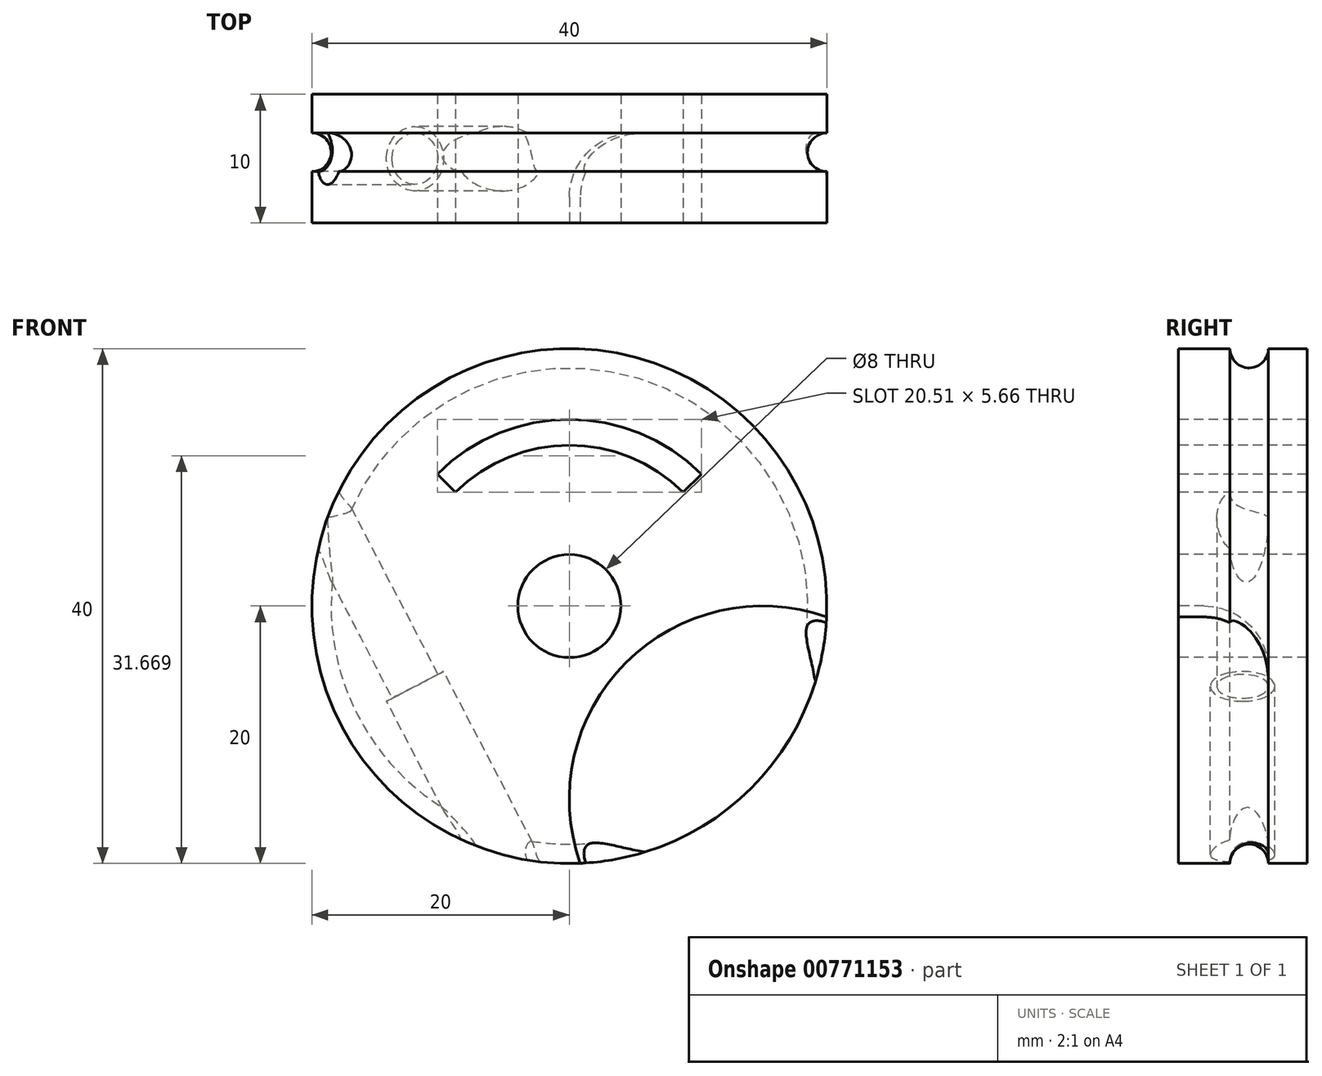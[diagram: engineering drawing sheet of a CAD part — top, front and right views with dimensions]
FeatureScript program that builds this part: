
annotation { "Feature Type Name" : "Feature", "Feature Type Description" : "" }
export const myFeature = defineFeature(function(context is Context, id is Id, definition is map)
    precondition{}
    {
        {
            var Q0;
            Q0=qCreatedBy(makeId("Front.planeOp"),FACE);
            var sketch = newSketch(context, id + "F0", { "sketchPlane" : qUnion([Q0])});
            skCircle(sketch, "E0", {"center": v(0, 0) * mm, "radius": 20 * mm});
            skCircle(sketch, "E1", {"center": v(0, 0) * mm, "radius": 10 * mm});
            skCircle(sketch, "E2", {"center": v(0, 0) * mm, "radius": 4 * mm});
            skCircle(sketch, "E3", {"center": v(0, 0) * mm, "radius": 18 * mm});
            skSolve(sketch);
        }
        {
            var Q0;
            Q0=makeQuery(id+"F0.imprint","IMPRINT",FACE,{"disambiguationData":[TD([[makeQuery(id+"F0.imprint","IMPRINT",EDGE,{"derivedFrom":sQuery(id+"F0.wireOp",EDGE,"E0")}),1.0]])]});
            var Q1;
            Q1=makeQuery(id+"F0.imprint","IMPRINT",FACE,{"disambiguationData":[TD([[makeQuery(id+"F0.imprint","IMPRINT",EDGE,{"derivedFrom":sQuery(id+"F0.wireOp",EDGE,"E1")}),1.0]])]});
            var Q2;
            Q2=makeQuery(id+"F0.imprint","IMPRINT",FACE,{"disambiguationData":[TD([[makeQuery(id+"F0.imprint","IMPRINT",EDGE,{"derivedFrom":sQuery(id+"F0.wireOp",EDGE,"E1")}),-1.0]])]});
            var Q3;
            Q3=makeQuery(id+"F0.imprint","IMPRINT",FACE,{"disambiguationData":[TD([[makeQuery(id+"F0.imprint","IMPRINT",EDGE,{"derivedFrom":sQuery(id+"F0.wireOp",EDGE,"E0")}),1.0]])]});
            extrude(context, id + "F1", {"entities" : qUnion([Q0, Q1, Q2, Q3]), "oppositeDirection" : true, "depth" : 3 * mm, "offsetDistance" : 25 * mm});
        }
        {
            var Q0;
            Q0=makeQuery(id+"F0.imprint","IMPRINT",FACE,{"disambiguationData":[TD([[makeQuery(id+"F0.imprint","IMPRINT",EDGE,{"derivedFrom":sQuery(id+"F0.wireOp",EDGE,"E0")}),1.0]])]});
            var Q1;
            Q1=makeQuery(id+"F0.imprint","IMPRINT",FACE,{"disambiguationData":[TD([[makeQuery(id+"F0.imprint","IMPRINT",EDGE,{"derivedFrom":sQuery(id+"F0.wireOp",EDGE,"E1")}),-1.0]])]});
            var Q2;
            Q2=makeQuery(id+"F0.imprint","IMPRINT",FACE,{"disambiguationData":[TD([[makeQuery(id+"F0.imprint","IMPRINT",EDGE,{"derivedFrom":sQuery(id+"F0.wireOp",EDGE,"E1")}),1.0]])]});
            extrude(context, id + "F2", {"entities" : qUnion([Q0, Q1, Q2]), "operationType" : NewBodyOperationType.ADD, "oppositeDirection" : true, "depth" : 3 * mm, "offsetDistance" : 25 * mm});
        }
        {
            var Q0;
            Q0=qCreatedBy(makeId("Front.planeOp"),FACE);
            cPlane(context, id + "F3", {"entities" : qUnion([Q0]), "cplaneType" : CPlaneType.OFFSET, "offset" : 15 * mm, "oppositeDirection" : true, "width" : 150 * mm, "height" : 150 * mm});
        }
        {
            var Q0;
            Q0=qCreatedBy(id+"F3.planeOp",FACE);
            var sketch = newSketch(context, id + "F4", { "sketchPlane" : qUnion([Q0])});
            skPoint(sketch, "E4.0", {"position": v(0, 0) * mm});
            skCircle(sketch, "E5.0", {"center": v(0, 0) * mm, "radius": 10 * mm});
            skCircle(sketch, "E5.1", {"center": v(0, 0) * mm, "radius": 20 * mm});
            skLineSegment(sketch, "E6", {"start": v(0, 10) * mm, "end": v(0, 115) * mm});
            skArc(sketch, "E7", {"start": v(55, 165) * mm, "mid": v(16.44, 152.17) * mm, "end": v(0, 115) * mm});
            skLineSegment(sketch, "E8", {"start": v(0, 115) * mm, "end": v(50.23, 115) * mm, "construction": true});
            skLineSegment(sketch, "E9", {"start": v(0, 115) * mm, "end": v(0, 165) * mm, "construction": true});
            skLineSegment(sketch, "E10", {"start": v(55, 165) * mm, "end": v(0, 165) * mm, "construction": true});
            skSolve(sketch);
        }
        {
            var Q0;
            Q0=qCreatedBy(makeId("Top.planeOp"),FACE);
            cPlane(context, id + "F5", {"entities" : qUnion([Q0]), "cplaneType" : CPlaneType.OFFSET, "offset" : 8 * mm, "width" : 150 * mm, "height" : 150 * mm});
        }
        {
            var Q0;
            Q0=makeQuery(id+"F0.imprint","IMPRINT",FACE,{"disambiguationData":[TD([[makeQuery(id+"F0.imprint","IMPRINT",EDGE,{"derivedFrom":sQuery(id+"F0.wireOp",EDGE,"E0")}),1.0]])]});
            var Q1;
            Q1=makeQuery(id+"F0.imprint","IMPRINT",FACE,{"disambiguationData":[TD([[makeQuery(id+"F0.imprint","IMPRINT",EDGE,{"derivedFrom":sQuery(id+"F0.wireOp",EDGE,"E1")}),-1.0]])]});
            var Q2;
            Q2=makeQuery(id+"F0.imprint","IMPRINT",FACE,{"disambiguationData":[TD([[makeQuery(id+"F0.imprint","IMPRINT",EDGE,{"derivedFrom":sQuery(id+"F0.wireOp",EDGE,"E1")}),1.0]])]});
            extrude(context, id + "F6", {"entities" : qUnion([Q0, Q1, Q2]), "operationType" : NewBodyOperationType.ADD, "depth" : 7 * mm, "offsetDistance" : 25 * mm});
        }
        {
            var Q0;
            Q0=qCreatedBy(makeId("Right.planeOp"),FACE);
            var sketch = newSketch(context, id + "F7", { "sketchPlane" : qUnion([Q0])});
            skCircle(sketch, "E11", {"center": v(-1.5, 20) * mm, "radius": 1.5 * mm});
            skSolve(sketch);
        }
        {
            var Q0;
            Q0=makeQuery(id+"F7.imprint","IMPRINT",FACE,{"disambiguationData":[TD([[makeQuery(id+"F7.imprint","IMPRINT",EDGE,{"derivedFrom":sQuery(id+"F7.wireOp",EDGE,"E11")}),1.0]])]});
            var Q1;
            Q1=makeQuery(id+"F6.opExtrude","CAP_EDGE",EDGE,{"disambiguationData":[OSD([sQuery(id+"F0.wireOp",EDGE,"E0")])],"isStart":false});
            revolve(context, id + "F8", {"operationType" : NewBodyOperationType.REMOVE, "surfaceOperationType" : NewSurfaceOperationType.NEW, "entities" : qUnion([Q0]), "axis" : qUnion([Q1]), "revolveType" : RevolveType.FULL, "oppositeDirection" : true});
        }
        {
            var Q0;
            Q0=makeQuery(id+"F6.opExtrude","CAP_FACE",FACE,{"disambiguationData":[OSD([sQuery(id+"F0.wireOp",EDGE,"E0"),sQuery(id+"F0.wireOp",EDGE,"E2")])],"isStart":false});
            cPlane(context, id + "F9", {"entities" : qUnion([Q0]), "cplaneType" : CPlaneType.OFFSET, "offset" : 0 * mm, "width" : 150 * mm, "height" : 150 * mm});
        }
        {
            var Q0;
            Q0=qCreatedBy(id+"F9.planeOp",FACE);
            var sketch = newSketch(context, id + "F10", { "sketchPlane" : qUnion([Q0])});
            skCircle(sketch, "E12", {"center": v(15, -15) * mm, "radius": 15 * mm});
            skLineSegment(sketch, "E13", {"start": v(0, 0) * mm, "end": v(50, 0) * mm});
            skLineSegment(sketch, "E14", {"start": v(0, 0) * mm, "end": v(0, -50) * mm});
            skCircle(sketch, "E15", {"center": v(0, 0) * mm, "radius": 12.5 * mm});
            skCircle(sketch, "E16", {"center": v(0, 0) * mm, "radius": 14.5 * mm});
            skLineSegment(sketch, "E17", {"start": v(0, 0) * mm, "end": v(-14.14, 14.14) * mm});
            skLineSegment(sketch, "E18", {"start": v(0, 0) * mm, "end": v(14.14, 14.14) * mm});
            skSolve(sketch);
        }
        {
            var Q0;
            Q0=qCreatedBy(id+"F9.planeOp",FACE);
            var sketch = newSketch(context, id + "F11", { "sketchPlane" : qUnion([Q0])});
            skLineSegment(sketch, "E19", {"start": v(0, 0) * mm, "end": v(-12.94, -48.3) * mm});
            skLineSegment(sketch, "E20", {"start": v(0, 0) * mm, "end": v(-46.98, 17.1) * mm});
            skCircle(sketch, "E21.0", {"center": v(0, 0) * mm, "radius": 20 * mm});
            skLineSegment(sketch, "E22", {"start": v(-18.8, 6.84) * mm, "end": v(-5.18, -19.32) * mm});
            skSolve(sketch);
        }
        {
            var Q0;
            Q0=qCreatedBy(id+"F9.planeOp",FACE);
            cPlane(context, id + "F12", {"entities" : qUnion([Q0]), "cplaneType" : CPlaneType.OFFSET, "offset" : 5 * mm, "oppositeDirection" : true, "width" : 150 * mm, "height" : 150 * mm});
        }
        {
            var Q0;
            Q0=qCreatedBy(id+"F12.planeOp",FACE);
            var sketch = newSketch(context, id + "F13", { "sketchPlane" : qUnion([Q0])});
            skPoint(sketch, "E23.0", {"position": v(-18.8, 6.84) * mm});
            skPoint(sketch, "E24.0", {"position": v(-5.18, -19.32) * mm});
            skLineSegment(sketch, "E25.0", {"start": v(-18.8, 6.84) * mm, "end": v(-5.18, -19.32) * mm});
            skSolve(sketch);
        }
        {
            var Q0;
            Q0=sQuery(id+"F13.wireOp",EDGE,"E25.0");
            cPlane(context, id + "F14", {"entities" : qUnion([Q0]), "cplaneType" : CPlaneType.MID_PLANE, "offset" : 25 * mm, "width" : 150 * mm, "height" : 150 * mm});
        }
        {
            var Q0;
            Q0=qCreatedBy(id+"F14.planeOp",FACE);
            var sketch = newSketch(context, id + "F15", { "sketchPlane" : qUnion([Q0])});
            skPoint(sketch, "E26.0", {"position": v(-13.51, 2) * mm});
            skCircle(sketch, "E27", {"center": v(-13.51, 2) * mm, "radius": 2 * mm});
            skCircle(sketch, "E28", {"center": v(-13.51, 2) * mm, "radius": 2.5 * mm});
            skSolve(sketch);
        }
        {
            var Q0;
            Q0=makeQuery(id+"F15.imprint","IMPRINT",FACE,{"disambiguationData":[TD([[makeQuery(id+"F15.imprint","IMPRINT",EDGE,{"derivedFrom":sQuery(id+"F15.wireOp",EDGE,"E27")}),1.0]])]});
            extrude(context, id + "F16", {"entities" : qUnion([Q0]), "operationType" : NewBodyOperationType.REMOVE, "oppositeDirection" : true, "depth" : 40 * mm, "offsetDistance" : 25 * mm, "symmetric" : true});
        }
        {
            var Q0;
            Q0=makeQuery(id+"F15.imprint","IMPRINT",FACE,{"disambiguationData":[TD([[makeQuery(id+"F15.imprint","IMPRINT",EDGE,{"derivedFrom":sQuery(id+"F15.wireOp",EDGE,"E27")}),-1.0]])]});
            var Q1;
            Q1=sQuery(id+"F15.wireOp",EDGE,"E28");
            var Q2;
            Q2=sQuery(id+"F15.wireOp",EDGE,"E27");
            extrude(context, id + "F17", {"entities" : qUnion([Q0]), "operationType" : NewBodyOperationType.REMOVE, "surfaceEntities" : qUnion([Q1, Q2]), "depth" : 25 * mm, "offsetDistance" : 25 * mm});
        }
        {
            var Q0;
            {var subQ0=sQuery(id+"F10.wireOp",EDGE,"E18");var subQ1=sQuery(id+"F10.wireOp",EDGE,"E15");var subQ2=makeQuery(id+"F10.imprint","INTERSECT",VERTEX,{"derivedFrom":[subQ1,subQ0]});Q0=makeQuery(id+"F10.imprint","IMPRINT",FACE,{"disambiguationData":[TD([[makeQuery(id+"F10.imprint","IMPRINT",EDGE,{"disambiguationData":[TD([[subQ2,-1.0]])],"derivedFrom":subQ1}),-1.0]])]});}
            extrude(context, id + "F18", {"entities" : qUnion([Q0]), "operationType" : NewBodyOperationType.REMOVE, "endBound" : BoundingType.THROUGH_ALL, "oppositeDirection" : true, "depth" : 25 * mm, "offsetDistance" : 25 * mm});
        }
        {
            var Q0;
            {var subQ0=sQuery(id+"F10.wireOp",EDGE,"815154f5-1ca3-4dbd-a51d-8ff744def0ee.0");var subQ1=sQuery(id+"F10.wireOp",EDGE,"E12");var subQ8=makeQuery(id+"F10.imprint","INTERSECT",VERTEX,{"disambiguationData":[OD(0.0)],"derivedFrom":[subQ1,subQ0]});Q0=makeQuery(id+"F10.imprint","IMPRINT",FACE,{"disambiguationData":[TD([[makeQuery(id+"F10.imprint","IMPRINT",EDGE,{"disambiguationData":[TD([[subQ8,-1.0]])],"derivedFrom":subQ1}),1.0]])]});}
            var Q1;
            {var subQ0=sQuery(id+"F10.wireOp",EDGE,"E15");var subQ1=sQuery(id+"F10.wireOp",EDGE,"E12");var subQ2=makeQuery(id+"F10.imprint","INTERSECT",VERTEX,{"disambiguationData":[OD(0.0)],"derivedFrom":[subQ1,subQ0]});Q1=makeQuery(id+"F10.imprint","IMPRINT",FACE,{"disambiguationData":[TD([[makeQuery(id+"F10.imprint","IMPRINT",EDGE,{"disambiguationData":[TD([[subQ2,-1.0]])],"derivedFrom":subQ1}),1.0]])]});}
            var Q2;
            {var subQ0=sQuery(id+"F10.wireOp",EDGE,"E12");var subQ1=makeQuery(id+"F10.imprint","INTERSECT",VERTEX,{"derivedFrom":[subQ0,sQuery(id+"F10.wireOp",EDGE,"E13")]});Q2=makeQuery(id+"F10.imprint","IMPRINT",FACE,{"disambiguationData":[TD([[makeQuery(id+"F10.imprint","IMPRINT",EDGE,{"disambiguationData":[TD([[subQ1,-1.0]])],"derivedFrom":subQ0}),1.0]])]});}
            var Q3;
            {var subQ0=sQuery(id+"F10.wireOp",EDGE,"E16");var subQ1=sQuery(id+"F10.wireOp",EDGE,"E12");var subQ2=makeQuery(id+"F10.imprint","INTERSECT",VERTEX,{"disambiguationData":[OD(0.0)],"derivedFrom":[subQ1,subQ0]});Q3=makeQuery(id+"F10.imprint","IMPRINT",FACE,{"disambiguationData":[TD([[makeQuery(id+"F10.imprint","IMPRINT",EDGE,{"disambiguationData":[TD([[subQ2,-1.0]])],"derivedFrom":subQ1}),1.0]])]});}
            extrude(context, id + "F19", {"entities" : qUnion([Q0, Q1, Q2, Q3]), "operationType" : NewBodyOperationType.REMOVE, "oppositeDirection" : true, "depth" : 7 * mm, "offsetDistance" : 25 * mm});
        }
        {
            var Q0;
            Q0=makeQuery(id+"F19.boolean.opBoolean","COPY",EDGE,{"derivedFrom":makeQuery(id+"F19.opExtrude","CAP_EDGE",EDGE,{"disambiguationData":[OSD([sQuery(id+"F10.wireOp",EDGE,"E12")])],"isStart":false})});
            fillet(context, id + "F20", {"entities" : qUnion([Q0]), "radius" : 5 * mm, "allowEdgeOverflow" : false});
        }
    });
